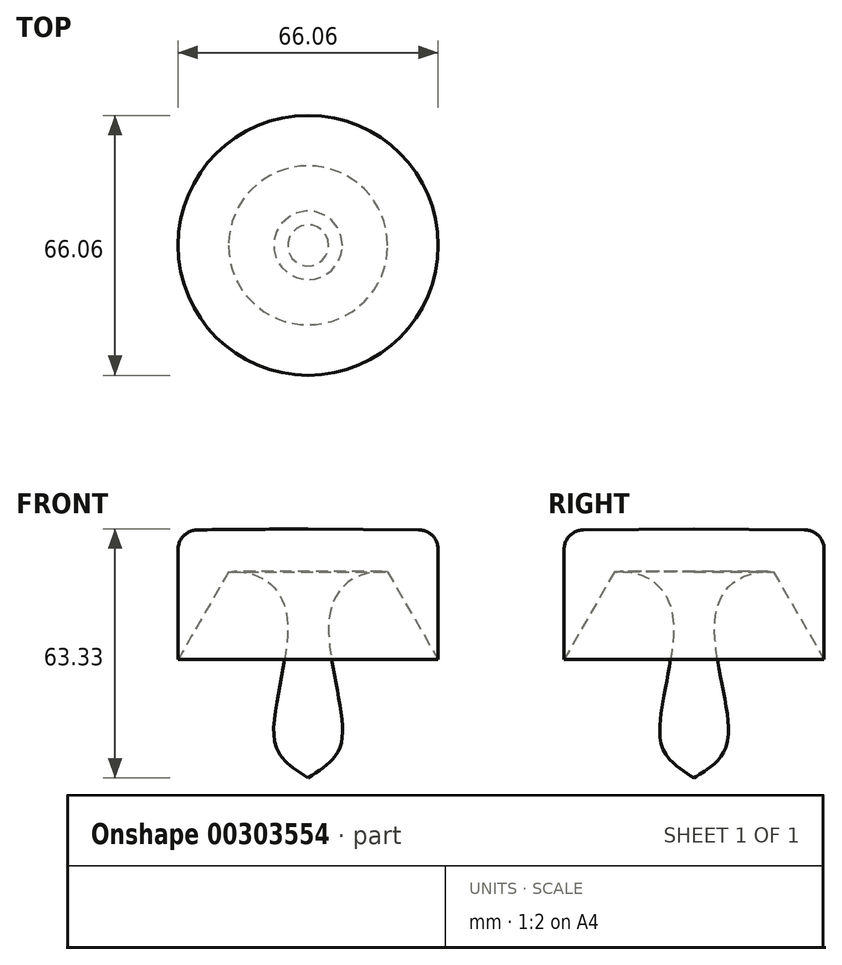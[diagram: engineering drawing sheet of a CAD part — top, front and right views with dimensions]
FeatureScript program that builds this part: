
annotation { "Feature Type Name" : "Feature", "Feature Type Description" : "" }
export const myFeature = defineFeature(function(context is Context, id is Id, definition is map)
    precondition{}
    {
        {
            var Q0;
            Q0=qCreatedBy(makeId("Front.planeOp"),FACE);
            var sketch = newSketch(context, id + "F0", { "sketchPlane" : qUnion([Q0])});
            skLineSegment(sketch, "E0", {"start": v(0, 0) * mm, "end": v(0, 63.33) * mm});
            skLineSegment(sketch, "E1", {"start": v(0, 63.33) * mm, "end": v(33.03, 63.05) * mm});
            skLineSegment(sketch, "E2", {"start": v(33.03, 63.05) * mm, "end": v(33.03, 30.19) * mm});
            skLineSegment(sketch, "E3", {"start": v(33.03, 30.19) * mm, "end": v(20.2, 52.4) * mm});
            skFitSpline(sketch, "E4", {"points": [v(20.2, 52.4) * mm, v(5.46, 41.35) * mm, v(8.46, 9.14) * mm, v(0, 0) * mm], "startDerivative": vector(-76.59, 5.34) * mm, "endDerivative": vector(-40.43, -28.74) * mm});
            skSolve(sketch);
        }
        {
            var Q0;
            Q0=makeQuery(id+"F0.imprint","IMPRINT",FACE,{"disambiguationData":[TD([[makeQuery(id+"F0.imprint","IMPRINT",EDGE,{"derivedFrom":sQuery(id+"F0.wireOp",EDGE,"E0")}),-1.0]])]});
            var Q1;
            Q1=sQuery(id+"F0.wireOp",EDGE,"E0");
            revolve(context, id + "F1", {"entities" : qUnion([Q0]), "axis" : qUnion([Q1]), "revolveType" : RevolveType.FULL});
        }
        {
            var Q0;
            Q0=makeQuery(id+"F1.opRevolve","SWEPT_FACE",FACE,{"disambiguationData":[OSD([sQuery(id+"F0.wireOp",EDGE,"E1")])]});
            fillet(context, id + "F2", {"entities" : qUnion([Q0]), "radius" : 5 * mm, "tangentPropagation" : true, "allowEdgeOverflow" : false});
        }
    });
